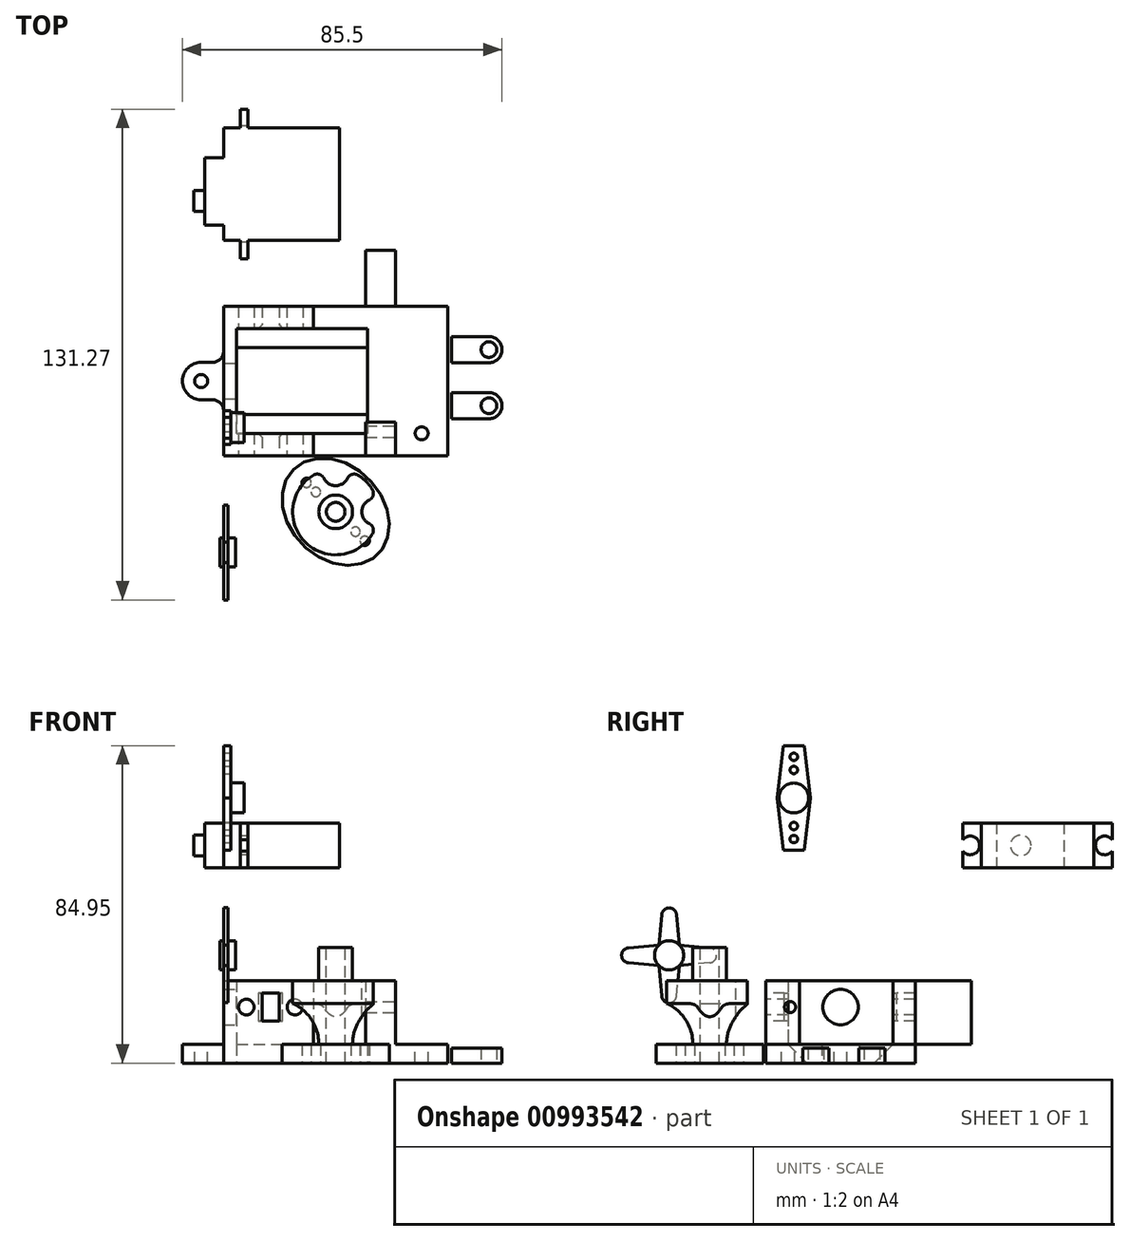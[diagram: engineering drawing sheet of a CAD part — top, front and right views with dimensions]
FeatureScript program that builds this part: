
annotation { "Feature Type Name" : "Feature", "Feature Type Description" : "" }
export const myFeature = defineFeature(function(context is Context, id is Id, definition is map)
    precondition{}
    {
        {
            assignVariable(context, id + "F0", {"variableType" : VariableType.LENGTH, "name" : "baseHgt", "lengthValue" : 17 * mm});
        }
        {
            assignVariable(context, id + "F1", {"variableType" : VariableType.LENGTH, "name" : "followerThk", "lengthValue" : 4 * mm});
        }
        {
            var Q0;
            Q0=qCreatedBy(makeId("Top.planeOp"),FACE);
            var sketch = newSketch(context, id + "F2", { "sketchPlane" : qUnion([Q0])});
            skLineSegment(sketch, "E0.bottom", {"start": v(0, 0) * mm, "end": v(60, 0) * mm});
            skLineSegment(sketch, "E0.top", {"start": v(0, 40) * mm, "end": v(60, 40) * mm});
            skLineSegment(sketch, "E0.left", {"start": v(0, 0) * mm, "end": v(0, 40) * mm});
            skLineSegment(sketch, "E0.right", {"start": v(60, 0) * mm, "end": v(60, 40) * mm});
            skLineSegment(sketch, "E1.bottom", {"start": v(30, 40) * mm, "end": v(60, 40) * mm});
            skLineSegment(sketch, "E1.top", {"start": v(30, 55) * mm, "end": v(60, 55) * mm});
            skLineSegment(sketch, "E1.left", {"start": v(30, 40) * mm, "end": v(30, 55) * mm});
            skLineSegment(sketch, "E1.right", {"start": v(60, 40) * mm, "end": v(60, 55) * mm});
            skLineSegment(sketch, "E2", {"start": v(0, 25) * mm, "end": v(-6, 25) * mm});
            skLineSegment(sketch, "E3", {"start": v(0, 15) * mm, "end": v(-6, 15) * mm});
            skArc(sketch, "E4", {"start": v(-6, 25) * mm, "mid": v(-11, 20) * mm, "end": v(-6, 15) * mm});
            skLineSegment(sketch, "E5", {"start": v(-6, 20) * mm, "end": v(0, 20) * mm, "construction": true});
            skSolve(sketch);
        }
        {
            var Q0;
            Q0=makeQuery(id+"F2.imprint","IMPRINT",FACE,{"disambiguationData":[TD([[makeQuery(id+"F2.imprint","IMPRINT",EDGE,{"derivedFrom":sQuery(id+"F2.wireOp",EDGE,"E0.bottom")}),1.0]])]});
            var Q1;
            Q1=makeQuery(id+"F2.imprint","IMPRINT",FACE,{"disambiguationData":[TD([[makeQuery(id+"F2.imprint","IMPRINT",EDGE,{"derivedFrom":sQuery(id+"F2.wireOp",EDGE,"E1.bottom")}),1.0]])]});
            var Q2;
            {var subQ0=sQuery(id+"F2.wireOp",EDGE,"E2");Q2=makeQuery(id+"F2.imprint","IMPRINT",FACE,{"disambiguationData":[TD([[makeQuery(id+"F2.imprint","IMPRINT",EDGE,{"derivedFrom":subQ0}),1.0]])]});}
            extrude(context, id + "F3", {"entities" : qUnion([Q0, Q1, Q2]), "depth" : 5 * mm, "offsetDistance" : 25 * mm});
        }
        {
            var Q0;
            Q0=makeQuery(id+"F3.opExtrude","CAP_FACE",FACE,{"disambiguationData":[OSD([sQuery(id+"F2.wireOp",EDGE,"E0.bottom"),sQuery(id+"F2.wireOp",EDGE,"E0.top"),sQuery(id+"F2.wireOp",EDGE,"E0.left"),sQuery(id+"F2.wireOp",EDGE,"E0.right")])],"isStart":false});
            var sketch = newSketch(context, id + "F4", { "sketchPlane" : qUnion([Q0])});
            skLineSegment(sketch, "E6", {"start": v(24, 0) * mm, "end": v(0, 0) * mm});
            skLineSegment(sketch, "E7", {"start": v(0, 0) * mm, "end": v(0, 40) * mm});
            skLineSegment(sketch, "E8", {"start": v(0, 40) * mm, "end": v(24, 40) * mm});
            skLineSegment(sketch, "E9", {"start": v(24, 40) * mm, "end": v(24, 34) * mm});
            skLineSegment(sketch, "E10", {"start": v(24, 34) * mm, "end": v(3.5, 34) * mm});
            skLineSegment(sketch, "E11", {"start": v(3.5, 34) * mm, "end": v(3.5, 6) * mm});
            skLineSegment(sketch, "E12", {"start": v(3.5, 6) * mm, "end": v(24, 6) * mm});
            skLineSegment(sketch, "E13", {"start": v(24, 6) * mm, "end": v(24, 0) * mm});
            skSolve(sketch);
        }
        {
            var Q0;
            Q0=makeQuery(id+"F4.imprint","IMPRINT",FACE,{"disambiguationData":[TD([[makeQuery(id+"F4.imprint","IMPRINT",EDGE,{"derivedFrom":sQuery(id+"F4.wireOp",EDGE,"E6")}),1.0]])]});
            extrude(context, id + "F5", {"entities" : qUnion([Q0]), "operationType" : NewBodyOperationType.ADD, "depth" : getVariable(context, 'baseHgt'), "offsetDistance" : 25 * mm});
        }
        {
            var Q0;
            Q0=makeQuery(id+"F5.opExtrude","SWEPT_FACE",FACE,{"disambiguationData":[OSD([sQuery(id+"F4.wireOp",EDGE,"E11")])]});
            var sketch = newSketch(context, id + "F6", { "sketchPlane" : qUnion([Q0])});
            skCircle(sketch, "E14", {"center": v(20, 15) * mm, "radius": 4.75 * mm});
            skLineSegment(sketch, "E15", {"start": v(20, 15) * mm, "end": v(20, 5) * mm, "construction": true});
            skSolve(sketch);
        }
        {
            var Q0;
            Q0 = qSketchRegion(id + "F6", true);
            extrude(context, id + "F7", {"entities" : qUnion([Q0]), "operationType" : NewBodyOperationType.REMOVE, "endBound" : BoundingType.THROUGH_ALL, "oppositeDirection" : true, "depth" : 25 * mm, "offsetDistance" : 25 * mm});
        }
        {
            var Q0;
            Q0=makeQuery(id+"F5.boolean.opBoolean","MERGE",FACE,{"derivedFrom":[makeQuery(id+"F3.opExtrude","SWEPT_FACE",FACE,{"disambiguationData":[OSD([sQuery(id+"F2.wireOp",EDGE,"E0.bottom")])]}),makeQuery(id+"F5.opExtrude","SWEPT_FACE",FACE,{"disambiguationData":[OSD([sQuery(id+"F4.wireOp",EDGE,"E6")])]})]});
            var sketch = newSketch(context, id + "F8", { "sketchPlane" : qUnion([Q0])});
            skLineSegment(sketch, "E16.bottom", {"start": v(10.35, 18.75) * mm, "end": v(14.85, 18.75) * mm});
            skLineSegment(sketch, "E16.top", {"start": v(10.35, 11.25) * mm, "end": v(14.85, 11.25) * mm});
            skLineSegment(sketch, "E16.left", {"start": v(10.35, 18.75) * mm, "end": v(10.35, 11.25) * mm});
            skLineSegment(sketch, "E16.right", {"start": v(14.85, 18.75) * mm, "end": v(14.85, 11.25) * mm});
            skLineSegment(sketch, "E17", {"start": v(10.35, 15) * mm, "end": v(6.1, 15) * mm, "construction": true});
            skLineSegment(sketch, "E18", {"start": v(14.85, 15) * mm, "end": v(19.1, 15) * mm, "construction": true});
            skCircle(sketch, "E19", {"center": v(6.1, 15) * mm, "radius": 2.1 * mm});
            skCircle(sketch, "E20", {"center": v(19.1, 15) * mm, "radius": 2.1 * mm});
            skLineSegment(sketch, "E21", {"start": v(4, 22) * mm, "end": v(4, 0) * mm, "construction": true});
            skLineSegment(sketch, "E22", {"start": v(3.5, 22) * mm, "end": v(3.5, 0) * mm, "construction": true});
            skSolve(sketch);
        }
        {
            var Q0;
            Q0 = qSketchRegion(id + "F8", true);
            extrude(context, id + "F9", {"entities" : qUnion([Q0]), "operationType" : NewBodyOperationType.REMOVE, "endBound" : BoundingType.THROUGH_ALL, "oppositeDirection" : true, "depth" : 25 * mm, "offsetDistance" : 25 * mm});
        }
        {
            var Q0;
            Q0=qCreatedBy(makeId("Right.planeOp"),FACE);
            var sketch = newSketch(context, id + "F10", { "sketchPlane" : qUnion([Q0])});
            skLineSegment(sketch, "E23.bottom", {"start": v(57.7, 52.25) * mm, "end": v(87.7, 52.25) * mm});
            skLineSegment(sketch, "E23.top", {"start": v(57.7, 64.25) * mm, "end": v(87.7, 64.25) * mm});
            skLineSegment(sketch, "E23.left", {"start": v(57.7, 52.25) * mm, "end": v(57.7, 64.25) * mm});
            skLineSegment(sketch, "E23.right", {"start": v(87.7, 52.25) * mm, "end": v(87.7, 64.25) * mm});
            skSolve(sketch);
        }
        {
            var Q0;
            Q0=makeQuery(id+"F10.imprint","IMPRINT",FACE,{"disambiguationData":[TD([[makeQuery(id+"F10.imprint","IMPRINT",EDGE,{"derivedFrom":sQuery(id+"F10.wireOp",EDGE,"E23.bottom")}),1.0]])]});
            extrude(context, id + "F11", {"entities" : qUnion([Q0]), "depth" : 31 * mm, "offsetDistance" : 25 * mm});
        }
        {
            var Q0;
            Q0=makeQuery(id+"F11.opExtrude","SWEPT_FACE",FACE,{"disambiguationData":[OSD([sQuery(id+"F10.wireOp",EDGE,"E23.left")])]});
            var sketch = newSketch(context, id + "F12", { "sketchPlane" : qUnion([Q0])});
            skLineSegment(sketch, "E24.bottom", {"start": v(4.5, 64.25) * mm, "end": v(6.5, 64.25) * mm});
            skLineSegment(sketch, "E24.top", {"start": v(4.5, 52.25) * mm, "end": v(6.5, 52.25) * mm});
            skLineSegment(sketch, "E24.left", {"start": v(4.5, 64.25) * mm, "end": v(4.5, 52.25) * mm});
            skLineSegment(sketch, "E24.right", {"start": v(6.5, 64.25) * mm, "end": v(6.5, 52.25) * mm});
            skSolve(sketch);
        }
        {
            var Q0;
            Q0 = qSketchRegion(id + "F12", true);
            extrude(context, id + "F13", {"entities" : qUnion([Q0]), "operationType" : NewBodyOperationType.ADD, "depth" : 5 * mm, "offsetDistance" : 25 * mm, "hasSecondDirection" : true, "secondDirectionOppositeDirection" : true, "secondDirectionDepth" : 35 * mm});
        }
        {
            var Q0;
            Q0=makeQuery(id+"F11.opExtrude","CAP_FACE",FACE,{"disambiguationData":[OSD([sQuery(id+"F10.wireOp",EDGE,"E23.bottom"),sQuery(id+"F10.wireOp",EDGE,"E23.top"),sQuery(id+"F10.wireOp",EDGE,"E23.left"),sQuery(id+"F10.wireOp",EDGE,"E23.right")])],"isStart":true});
            var sketch = newSketch(context, id + "F14", { "sketchPlane" : qUnion([Q0])});
            skLineSegment(sketch, "E25.bottom", {"start": v(-79.7, 64.25) * mm, "end": v(-61.7, 64.25) * mm});
            skLineSegment(sketch, "E25.top", {"start": v(-79.7, 52.25) * mm, "end": v(-61.7, 52.25) * mm});
            skLineSegment(sketch, "E25.left", {"start": v(-79.7, 64.25) * mm, "end": v(-79.7, 52.25) * mm});
            skLineSegment(sketch, "E25.right", {"start": v(-61.7, 64.25) * mm, "end": v(-61.7, 52.25) * mm});
            skSolve(sketch);
        }
        {
            var Q0;
            Q0=makeQuery(id+"F14.imprint","IMPRINT",FACE,{"disambiguationData":[TD([[makeQuery(id+"F14.imprint","IMPRINT",EDGE,{"derivedFrom":sQuery(id+"F14.wireOp",EDGE,"E25.bottom")}),1.0]])]});
            extrude(context, id + "F15", {"entities" : qUnion([Q0]), "operationType" : NewBodyOperationType.ADD, "depth" : 5 * mm, "offsetDistance" : 25 * mm});
        }
        {
            var Q0;
            Q0=makeQuery(id+"F15.opExtrude","CAP_FACE",FACE,{"disambiguationData":[OSD([sQuery(id+"F14.wireOp",EDGE,"E25.bottom"),sQuery(id+"F14.wireOp",EDGE,"E25.top"),sQuery(id+"F14.wireOp",EDGE,"E25.left"),sQuery(id+"F14.wireOp",EDGE,"E25.right")])],"isStart":false});
            var sketch = newSketch(context, id + "F16", { "sketchPlane" : qUnion([Q0])});
            skCircle(sketch, "E26", {"center": v(-68.2, 58.25) * mm, "radius": 2.75 * mm});
            skLineSegment(sketch, "E27", {"start": v(-79.7, 58.25) * mm, "end": v(-68.2, 58.25) * mm, "construction": true});
            skLineSegment(sketch, "E28.0", {"start": v(-57.7, 52.25) * mm, "end": v(-57.7, 64.25) * mm, "construction": true});
            skSolve(sketch);
        }
        {
            var Q0;
            Q0=makeQuery(id+"F16.imprint","IMPRINT",FACE,{"disambiguationData":[TD([[makeQuery(id+"F16.imprint","IMPRINT",EDGE,{"derivedFrom":sQuery(id+"F16.wireOp",EDGE,"E26")}),1.0]])]});
            extrude(context, id + "F17", {"entities" : qUnion([Q0]), "operationType" : NewBodyOperationType.ADD, "depth" : 3 * mm, "offsetDistance" : 25 * mm});
        }
        {
            var Q0;
            Q0=qCreatedBy(makeId("Right.planeOp"),FACE);
            var sketch = newSketch(context, id + "F18", { "sketchPlane" : qUnion([Q0])});
            skLineSegment(sketch, "E29", {"start": v(-27.87, 39.72) * mm, "end": v(-28.62, 31.6) * mm});
            skLineSegment(sketch, "E30", {"start": v(-25.87, 41.55) * mm, "end": v(-25.87, 28.85) * mm});
            skArc(sketch, "E31", {"start": v(-25.87, 41.55) * mm, "mid": v(-27.22, 41.02) * mm, "end": v(-27.87, 39.72) * mm});
            skLineSegment(sketch, "E32", {"start": v(-25.87, 28.85) * mm, "end": v(-38.57, 28.85) * mm});
            skArc(sketch, "E33", {"start": v(-36.74, 30.85) * mm, "mid": v(-38.04, 30.2) * mm, "end": v(-38.57, 28.85) * mm});
            skLineSegment(sketch, "E34", {"start": v(-25.87, 41.55) * mm, "end": v(-19.8, 41.55) * mm, "construction": true});
            skLineSegment(sketch, "E35", {"start": v(-38.57, 28.85) * mm, "end": v(-38.57, 21.53) * mm, "construction": true});
            skLineSegment(sketch, "E36", {"start": v(-36.74, 30.85) * mm, "end": v(-28.62, 31.6) * mm});
            skCircle(sketch, "E37", {"center": v(-25.87, 28.85) * mm, "radius": 12.7 * mm, "construction": true});
            skSolve(sketch);
        }
        {
            var Q0;
            Q0=makeQuery(id+"F18.imprint","IMPRINT",FACE,{"disambiguationData":[TD([[makeQuery(id+"F18.imprint","IMPRINT",EDGE,{"derivedFrom":sQuery(id+"F18.wireOp",EDGE,"E29")}),1.0]])]});
            extrude(context, id + "F19", {"entities" : qUnion([Q0]), "depth" : 1.2 * mm, "offsetDistance" : 25 * mm});
        }
        {
            var Q0;
            Q0=makeQuery(id+"F19.opExtrude","SWEPT_BODY",BODY,{"disambiguationData":[OSD([sQuery(id+"F18.wireOp",EDGE,"E29"),sQuery(id+"F18.wireOp",EDGE,"E30"),sQuery(id+"F18.wireOp",EDGE,"E31"),sQuery(id+"F18.wireOp",EDGE,"E32"),sQuery(id+"F18.wireOp",EDGE,"E33"),sQuery(id+"F18.wireOp",EDGE,"E36")])]});
            var Q1;
            Q1=makeQuery(id+"F19.opExtrude","SWEPT_EDGE",EDGE,{"disambiguationData":[OSD([sQuery(id+"F18.wireOp",EDGE,"E30"),sQuery(id+"F18.wireOp",EDGE,"E32")])]});
            circularPattern(context, id + "F20", {"operationType" : NewBodyOperationType.ADD, "entities" : qUnion([Q0]), "axis" : qUnion([Q1]), "angle" : 360 * degree, "instanceCount" : 4, "equalSpace" : true});
        }
        {
            var Q0;
            {var subQ0=makeQuery(id+"F19.opExtrude","CAP_FACE",FACE,{"disambiguationData":[OSD([sQuery(id+"F18.wireOp",EDGE,"E29"),sQuery(id+"F18.wireOp",EDGE,"E30"),sQuery(id+"F18.wireOp",EDGE,"E31"),sQuery(id+"F18.wireOp",EDGE,"E32"),sQuery(id+"F18.wireOp",EDGE,"E33"),sQuery(id+"F18.wireOp",EDGE,"E36")])],"isStart":false});Q0=makeQuery(id+"F20.boolean.opBoolean","MERGE",FACE,{"derivedFrom":[subQ0,makeQuery(id+"F20.opPattern","COPY",FACE,{"derivedFrom":subQ0,"instanceName":"1"}),makeQuery(id+"F20.opPattern","COPY",FACE,{"derivedFrom":subQ0,"instanceName":"2"}),makeQuery(id+"F20.opPattern","COPY",FACE,{"derivedFrom":subQ0,"instanceName":"3"})]});}
            var sketch = newSketch(context, id + "F21", { "sketchPlane" : qUnion([Q0])});
            skLineSegment(sketch, "E38", {"start": v(-23.12, 31.6) * mm, "end": v(-28.62, 26.1) * mm, "construction": true});
            skCircle(sketch, "E39", {"center": v(-25.87, 28.85) * mm, "radius": 3.9 * mm});
            skSolve(sketch);
        }
        {
            var Q0;
            Q0 = qSketchRegion(id + "F21", true);
            extrude(context, id + "F22", {"entities" : qUnion([Q0]), "operationType" : NewBodyOperationType.ADD, "depth" : 2 * mm, "offsetDistance" : 25 * mm, "hasSecondDirection" : true, "secondDirectionOppositeDirection" : true, "secondDirectionDepth" : 2.2 * mm});
        }
        {
            var Q0;
            {var subQ1=sQuery(id+"F12.wireOp",EDGE,"E24.left");Q0=makeQuery(id+"F13.boolean.opBoolean","SPLIT",FACE,{"disambiguationData":[TD([makeQuery(id+"F11.opExtrude","SWEPT_FACE",FACE,{"disambiguationData":[OSD([sQuery(id+"F10.wireOp",EDGE,"E23.right")])]})])],"derivedFrom":makeQuery(id+"F13.opExtrude","SWEPT_FACE",FACE,{"disambiguationData":[OSD([subQ1])]})});}
            var sketch = newSketch(context, id + "F23", { "sketchPlane" : qUnion([Q0])});
            skPoint(sketch, "E40", {"position": v(-90.7, 58.25) * mm});
            skPoint(sketch, "E41", {"position": v(-54.7, 58.25) * mm});
            skLineSegment(sketch, "E42", {"start": v(-92.7, 58.25) * mm, "end": v(-90.7, 58.25) * mm, "construction": true});
            skLineSegment(sketch, "E43.0", {"start": v(-52.7, 64.25) * mm, "end": v(-52.7, 52.25) * mm, "construction": true});
            skLineSegment(sketch, "E44", {"start": v(-54.7, 58.25) * mm, "end": v(-52.7, 58.25) * mm, "construction": true});
            skCircle(sketch, "E45", {"center": v(-90.7, 58.25) * mm, "radius": 2.5 * mm});
            skCircle(sketch, "E46", {"center": v(-54.7, 58.25) * mm, "radius": 2.5 * mm});
            skSolve(sketch);
        }
        {
            var Q0;
            {var subQ0=sQuery(id+"F23.wireOp",EDGE,"E45");var subQ1=makeQuery(id+"F13.opExtrude","CAP_EDGE",EDGE,{"disambiguationData":[OSD([sQuery(id+"F12.wireOp",EDGE,"E24.left")])],"isStart":true});var subQ2=makeQuery(id+"F23.imprint","INTERSECT",VERTEX,{"disambiguationData":[OD(0.0)],"derivedFrom":[subQ1,subQ0]});Q0=makeQuery(id+"F23.imprint","IMPRINT",FACE,{"disambiguationData":[TD([[makeQuery(id+"F23.imprint","IMPRINT",EDGE,{"disambiguationData":[TD([[subQ2,1.0]])],"derivedFrom":subQ0}),1.0]])]});}
            var Q1;
            Q1=makeQuery(id+"F23.imprint","IMPRINT",FACE,{"disambiguationData":[TD([[makeQuery(id+"F23.imprint","IMPRINT",EDGE,{"derivedFrom":sQuery(id+"F23.wireOp",EDGE,"E46")}),1.0]])]});
            extrude(context, id + "F24", {"entities" : qUnion([Q0, Q1]), "operationType" : NewBodyOperationType.REMOVE, "endBound" : BoundingType.THROUGH_ALL, "oppositeDirection" : true, "depth" : 25 * mm, "offsetDistance" : 25 * mm});
        }
        {
            var Q0;
            Q0=makeQuery(id+"F3.opExtrude","CAP_FACE",FACE,{"disambiguationData":[OSD([sQuery(id+"F2.wireOp",EDGE,"E0.bottom"),sQuery(id+"F2.wireOp",EDGE,"E0.top"),sQuery(id+"F2.wireOp",EDGE,"E0.left"),sQuery(id+"F2.wireOp",EDGE,"E0.right"),sQuery(id+"F2.wireOp",EDGE,"E1.top"),sQuery(id+"F2.wireOp",EDGE,"E1.left"),sQuery(id+"F2.wireOp",EDGE,"E1.right")])],"isStart":false});
            var sketch = newSketch(context, id + "F25", { "sketchPlane" : qUnion([Q0])});
            skLineSegment(sketch, "E47.bottom", {"start": v(38, 0) * mm, "end": v(46, 0) * mm});
            skLineSegment(sketch, "E47.top", {"start": v(38, 9) * mm, "end": v(46, 9) * mm});
            skLineSegment(sketch, "E47.left", {"start": v(38, 0) * mm, "end": v(38, 9) * mm});
            skLineSegment(sketch, "E47.right", {"start": v(46, 0) * mm, "end": v(46, 9) * mm});
            skLineSegment(sketch, "E48.bottom", {"start": v(38, 55) * mm, "end": v(46, 55) * mm});
            skLineSegment(sketch, "E48.top", {"start": v(38, 40) * mm, "end": v(46, 40) * mm});
            skLineSegment(sketch, "E48.left", {"start": v(38, 55) * mm, "end": v(38, 40) * mm});
            skLineSegment(sketch, "E48.right", {"start": v(46, 55) * mm, "end": v(46, 40) * mm});
            skSolve(sketch);
        }
        {
            var Q0;
            Q0=makeQuery(id+"F25.imprint","IMPRINT",FACE,{"disambiguationData":[TD([[makeQuery(id+"F25.imprint","IMPRINT",EDGE,{"derivedFrom":sQuery(id+"F25.wireOp",EDGE,"E47.bottom")}),1.0]])]});
            var Q1;
            Q1=makeQuery(id+"F25.imprint","IMPRINT",FACE,{"disambiguationData":[TD([[makeQuery(id+"F25.imprint","IMPRINT",EDGE,{"derivedFrom":sQuery(id+"F25.wireOp",EDGE,"E48.bottom")}),-1.0]])]});
            extrude(context, id + "F26", {"entities" : qUnion([Q0, Q1]), "operationType" : NewBodyOperationType.ADD, "depth" : getVariable(context, 'baseHgt'), "offsetDistance" : 25 * mm});
        }
        {
            var Q0;
            Q0=qCreatedBy(makeId("Right.planeOp"),FACE);
            var sketch = newSketch(context, id + "F27", { "sketchPlane" : qUnion([Q0])});
            skLineSegment(sketch, "E49", {"start": v(5.72, 92.95) * mm, "end": v(9.28, 92.95) * mm, "construction": true});
            skLineSegment(sketch, "E50", {"start": v(3, 70.95) * mm, "end": v(12, 70.95) * mm, "construction": true});
            skLineSegment(sketch, "E51", {"start": v(7.5, 92.95) * mm, "end": v(7.5, 70.95) * mm, "construction": true});
            skLineSegment(sketch, "E52", {"start": v(3, 70.95) * mm, "end": v(4.73, 84.95) * mm});
            skLineSegment(sketch, "E53", {"start": v(4.73, 84.95) * mm, "end": v(5.72, 92.95) * mm, "construction": true});
            skLineSegment(sketch, "E54", {"start": v(12, 70.95) * mm, "end": v(10.27, 84.95) * mm});
            skLineSegment(sketch, "E55", {"start": v(10.27, 84.95) * mm, "end": v(9.28, 92.95) * mm, "construction": true});
            skArc(sketch, "E56", {"start": v(9.5, 91.18) * mm, "mid": v(7.5, 92.95) * mm, "end": v(5.5, 91.18) * mm, "construction": true});
            skLineSegment(sketch, "E57.MirrorCS", {"start": v(3, 70.95) * mm, "end": v(4.73, 56.95) * mm});
            skLineSegment(sketch, "E58.MirrorCS", {"start": v(12, 70.95) * mm, "end": v(10.27, 56.95) * mm});
            skLineSegment(sketch, "E59", {"start": v(4.73, 56.95) * mm, "end": v(10.27, 56.95) * mm});
            skLineSegment(sketch, "E60", {"start": v(4.73, 84.95) * mm, "end": v(10.27, 84.95) * mm});
            skSolve(sketch);
        }
        {
            var Q0;
            Q0 = qSketchRegion(id + "F27", true);
            extrude(context, id + "F28", {"entities" : qUnion([Q0]), "depth" : 2 * mm, "offsetDistance" : 25 * mm});
        }
        {
            var Q0;
            Q0=makeQuery(id+"F28.opExtrude","CAP_FACE",FACE,{"disambiguationData":[OSD([sQuery(id+"F27.wireOp",EDGE,"E52"),sQuery(id+"F27.wireOp",EDGE,"E54"),sQuery(id+"F27.wireOp",EDGE,"E57.MirrorCS"),sQuery(id+"F27.wireOp",EDGE,"E58.MirrorCS"),sQuery(id+"F27.wireOp",EDGE,"E59"),sQuery(id+"F27.wireOp",EDGE,"E60")])],"isStart":false});
            var sketch = newSketch(context, id + "F29", { "sketchPlane" : qUnion([Q0])});
            skLineSegment(sketch, "E61", {"start": v(7.5, 84.95) * mm, "end": v(7.5, 56.95) * mm, "construction": true});
            skPoint(sketch, "E62", {"position": v(7.5, 78.45) * mm});
            skPoint(sketch, "E63", {"position": v(7.5, 63.45) * mm});
            skLineSegment(sketch, "E64", {"start": v(3, 70.95) * mm, "end": v(12, 70.95) * mm, "construction": true});
            skCircle(sketch, "E65", {"center": v(7.5, 78.45) * mm, "radius": 1 * mm});
            skCircle(sketch, "E66", {"center": v(7.5, 63.45) * mm, "radius": 1 * mm});
            skCircle(sketch, "E67", {"center": v(7.5, 81.95) * mm, "radius": 1 * mm});
            skCircle(sketch, "E68", {"center": v(7.5, 59.95) * mm, "radius": 1 * mm});
            skSolve(sketch);
        }
        {
            var Q0;
            Q0 = qSketchRegion(id + "F29", true);
            extrude(context, id + "F30", {"entities" : qUnion([Q0]), "operationType" : NewBodyOperationType.REMOVE, "endBound" : BoundingType.THROUGH_ALL, "oppositeDirection" : true, "depth" : 25 * mm, "offsetDistance" : 25 * mm});
        }
        {
            var Q0;
            Q0=makeQuery(id+"F28.opExtrude","CAP_FACE",FACE,{"disambiguationData":[OSD([sQuery(id+"F27.wireOp",EDGE,"E52"),sQuery(id+"F27.wireOp",EDGE,"E54"),sQuery(id+"F27.wireOp",EDGE,"E57.MirrorCS"),sQuery(id+"F27.wireOp",EDGE,"E58.MirrorCS"),sQuery(id+"F27.wireOp",EDGE,"E59"),sQuery(id+"F27.wireOp",EDGE,"E60")])],"isStart":false});
            var sketch = newSketch(context, id + "F31", { "sketchPlane" : qUnion([Q0])});
            skCircle(sketch, "E69", {"center": v(7.5, 70.95) * mm, "radius": 4 * mm});
            skPoint(sketch, "E69.centerSnap0", {"position": v(7.5, 84.95) * mm});
            skSolve(sketch);
        }
        {
            var Q0;
            Q0 = qSketchRegion(id + "F31", true);
            extrude(context, id + "F32", {"entities" : qUnion([Q0]), "operationType" : NewBodyOperationType.ADD, "depth" : 3.5 * mm, "offsetDistance" : 25 * mm});
        }
        {
            assignVariable(context, id + "F33", {"variableType" : VariableType.LENGTH, "name" : "camIndentFillet", "lengthValue" : 2 * mm});
        }
        {
            var Q0;
            Q0=qCreatedBy(makeId("Front.planeOp"),FACE);
            cPlane(context, id + "F34", {"entities" : qUnion([Q0]), "cplaneType" : CPlaneType.OFFSET, "offset" : 15 * mm, "width" : 150 * mm, "height" : 150 * mm});
        }
        {
            var Q0;
            Q0=qCreatedBy(id+"F34.planeOp",FACE);
            var sketch = newSketch(context, id + "F35", { "sketchPlane" : qUnion([Q0])});
            skLineSegment(sketch, "E70", {"start": v(30, 0) * mm, "end": v(42.5, 0) * mm});
            skLineSegment(sketch, "E71", {"start": v(42.5, 0) * mm, "end": v(42.5, 5) * mm});
            skLineSegment(sketch, "E72", {"start": v(42.5, 5) * mm, "end": v(34.5, 5) * mm});
            skArc(sketch, "E73", {"start": v(41.5, 16) * mm, "mid": v(36.4, 11.52) * mm, "end": v(34.5, 5) * mm});
            skLineSegment(sketch, "E74", {"start": v(34.5, 5) * mm, "end": v(34.5, 13) * mm, "construction": true});
            skLineSegment(sketch, "E75", {"start": v(41.5, 16) * mm, "end": v(41.5, 22) * mm});
            skLineSegment(sketch, "E76", {"start": v(41.5, 22) * mm, "end": v(34.5, 22) * mm});
            skLineSegment(sketch, "E77", {"start": v(34.5, 22) * mm, "end": v(34.5, 31) * mm});
            skLineSegment(sketch, "E78", {"start": v(30, 0) * mm, "end": v(30, 31) * mm});
            skLineSegment(sketch, "E79", {"start": v(30, 31) * mm, "end": v(34.5, 31) * mm});
            skSolve(sketch);
        }
        {
            var Q0;
            Q0 = qSketchRegion(id + "F35", true);
            var Q1;
            Q1=sQuery(id+"F35.wireOp",EDGE,"E78");
            revolve(context, id + "F36", {"surfaceOperationType" : NewSurfaceOperationType.NEW, "entities" : qUnion([Q0]), "axis" : qUnion([Q1]), "revolveType" : RevolveType.FULL});
        }
        {
            var Q0;
            Q0=makeQuery(id+"F36.opRevolve","SWEPT_FACE",FACE,{"disambiguationData":[OSD([sQuery(id+"F35.wireOp",EDGE,"E76")])]});
            var sketch = newSketch(context, id + "F37", { "sketchPlane" : qUnion([Q0])});
            skCircle(sketch, "E80", {"center": v(30, -4.5) * mm, "radius": 3.5 * mm});
            skCircle(sketch, "E81", {"center": v(40.5, -15) * mm, "radius": 3.5 * mm});
            skLineSegment(sketch, "E82", {"start": v(30, -4.5) * mm, "end": v(30, -15) * mm, "construction": true});
            skLineSegment(sketch, "E83", {"start": v(30, -15) * mm, "end": v(40.5, -15) * mm, "construction": true});
            skSolve(sketch);
        }
        {
            var Q0;
            Q0 = qSketchRegion(id + "F37", true);
            var Q1;
            Q1=makeQuery(id+"F36.opRevolve","SWEPT_FACE",FACE,{"disambiguationData":[OSD([sQuery(id+"F35.wireOp",EDGE,"E73")])]});
            extrude(context, id + "F38", {"entities" : qUnion([Q0]), "operationType" : NewBodyOperationType.REMOVE, "endBound" : BoundingType.UP_TO_SURFACE, "oppositeDirection" : true, "depth" : 25 * mm, "endBoundEntityFace" : qUnion([Q1]), "offsetDistance" : 25 * mm});
        }
        {
            var Q0;
            Q0=makeQuery(id+"F38.boolean.opBoolean","INTERSECT",EDGE,{"disambiguationData":[OD(0.0)],"derivedFrom":[makeQuery(id+"F36.opRevolve","SWEPT_FACE",FACE,{"disambiguationData":[OSD([sQuery(id+"F35.wireOp",EDGE,"E75")])]}),makeQuery(id+"F38.opExtrude","SWEPT_FACE",FACE,{"disambiguationData":[OSD([sQuery(id+"F37.wireOp",EDGE,"E80")])]})]});
            var Q1;
            Q1=makeQuery(id+"F38.boolean.opBoolean","INTERSECT",EDGE,{"disambiguationData":[OD(1.0)],"derivedFrom":[makeQuery(id+"F36.opRevolve","SWEPT_FACE",FACE,{"disambiguationData":[OSD([sQuery(id+"F35.wireOp",EDGE,"E75")])]}),makeQuery(id+"F38.opExtrude","SWEPT_FACE",FACE,{"disambiguationData":[OSD([sQuery(id+"F37.wireOp",EDGE,"E80")])]})]});
            var Q2;
            Q2=makeQuery(id+"F38.boolean.opBoolean","INTERSECT",EDGE,{"disambiguationData":[OD(0.0)],"derivedFrom":[makeQuery(id+"F36.opRevolve","SWEPT_FACE",FACE,{"disambiguationData":[OSD([sQuery(id+"F35.wireOp",EDGE,"E75")])]}),makeQuery(id+"F38.opExtrude","SWEPT_FACE",FACE,{"disambiguationData":[OSD([sQuery(id+"F37.wireOp",EDGE,"E81")])]})]});
            var Q3;
            Q3=makeQuery(id+"F38.boolean.opBoolean","INTERSECT",EDGE,{"disambiguationData":[OD(1.0)],"derivedFrom":[makeQuery(id+"F36.opRevolve","SWEPT_FACE",FACE,{"disambiguationData":[OSD([sQuery(id+"F35.wireOp",EDGE,"E75")])]}),makeQuery(id+"F38.opExtrude","SWEPT_FACE",FACE,{"disambiguationData":[OSD([sQuery(id+"F37.wireOp",EDGE,"E81")])]})]});
            fillet(context, id + "F39", {"entities" : qUnion([Q0, Q1, Q2, Q3]), "radius" : getVariable(context, 'camIndentFillet'), "tangentPropagation" : true, "allowEdgeOverflow" : false});
        }
        {
            var Q0;
            Q0=makeQuery(id+"F36.opRevolve","SWEPT_FACE",FACE,{"disambiguationData":[OSD([sQuery(id+"F35.wireOp",EDGE,"E70")])]});
            var sketch = newSketch(context, id + "F40", { "sketchPlane" : qUnion([Q0])});
            skEllipse(sketch, "E84", {"center": v(30, 15) * mm, "majorRadius": 12.5 * mm, "minorRadius": 16 * mm, "majorAxis": v(-0.7, 0.7)});
            skLineSegment(sketch, "E85", {"start": v(30, 15) * mm, "end": v(38.84, 6.16) * mm, "construction": true});
            skLineSegment(sketch, "E86", {"start": v(30, 15) * mm, "end": v(18.69, 3.69) * mm, "construction": true});
            skLineSegment(sketch, "E87", {"start": v(30, 15) * mm, "end": v(-10, 15) * mm, "construction": true});
            skSolve(sketch);
        }
        {
            var Q0;
            Q0 = qSketchRegion(id + "F40", true);
            var Q1;
            Q1=makeQuery(id+"F36.opRevolve","SWEPT_FACE",FACE,{"disambiguationData":[OSD([sQuery(id+"F35.wireOp",EDGE,"E72")])]});
            extrude(context, id + "F41", {"entities" : qUnion([Q0]), "operationType" : NewBodyOperationType.ADD, "endBound" : BoundingType.UP_TO_SURFACE, "oppositeDirection" : true, "depth" : 25 * mm, "endBoundEntityFace" : qUnion([Q1]), "offsetDistance" : 25 * mm});
        }
        {
            var Q0;
            Q0=makeQuery(id+"F36.opRevolve","SWEPT_FACE",FACE,{"disambiguationData":[OSD([sQuery(id+"F35.wireOp",EDGE,"E79")])]});
            var sketch = newSketch(context, id + "F42", { "sketchPlane" : qUnion([Q0])});
            skCircle(sketch, "E88", {"center": v(30, -15) * mm, "radius": 2.5 * mm});
            skSolve(sketch);
        }
        {
            var Q0;
            Q0 = qSketchRegion(id + "F42", true);
            extrude(context, id + "F43", {"entities" : qUnion([Q0]), "operationType" : NewBodyOperationType.REMOVE, "endBound" : BoundingType.THROUGH_ALL, "oppositeDirection" : true, "depth" : 25 * mm, "offsetDistance" : 25 * mm});
        }
        {
            var Q0;
            Q0=makeQuery(id+"F41.boolean.opBoolean","MERGE",FACE,{"derivedFrom":[makeQuery(id+"F36.opRevolve","SWEPT_FACE",FACE,{"disambiguationData":[OSD([sQuery(id+"F35.wireOp",EDGE,"E70")])]}),makeQuery(id+"F41.opExtrude","CAP_FACE",FACE,{"disambiguationData":[OSD([sQuery(id+"F40.wireOp",EDGE,"E84")])],"isStart":true})]});
            var sketch = newSketch(context, id + "F44", { "sketchPlane" : qUnion([Q0])});
            skLineSegment(sketch, "E89", {"start": v(41.31, 26.31) * mm, "end": v(18.69, 3.69) * mm, "construction": true});
            skLineSegment(sketch, "E90", {"start": v(21.16, 23.84) * mm, "end": v(38.84, 6.16) * mm, "construction": true});
            skPoint(sketch, "E91", {"position": v(22.22, 7.22) * mm});
            skPoint(sketch, "E92", {"position": v(37.78, 22.78) * mm});
            skPoint(sketch, "E93", {"position": v(35.3, 20.3) * mm});
            skPoint(sketch, "E94", {"position": v(24.7, 9.7) * mm});
            skSolve(sketch);
        }
        {
            var Q0;
            Q0=sQuery(id+"F44.wireOp",VERTEX,"E91");
            var Q1;
            Q1=sQuery(id+"F44.wireOp",VERTEX,"E92");
            var Q2;
            Q2=sQuery(id+"F44.wireOp",VERTEX,"E93");
            var Q3;
            Q3=sQuery(id+"F44.wireOp",VERTEX,"E94");
            var Q4;
            Q4=makeQuery(id+"F36.opRevolve","SWEPT_BODY",BODY,{"disambiguationData":[OSD([sQuery(id+"F35.wireOp",EDGE,"E70"),sQuery(id+"F35.wireOp",EDGE,"E71"),sQuery(id+"F35.wireOp",EDGE,"E72"),sQuery(id+"F35.wireOp",EDGE,"E73"),sQuery(id+"F35.wireOp",EDGE,"E75"),sQuery(id+"F35.wireOp",EDGE,"E76"),sQuery(id+"F35.wireOp",EDGE,"E77"),sQuery(id+"F35.wireOp",EDGE,"E78"),sQuery(id+"F35.wireOp",EDGE,"E79")])]});
            hole(context, id + "F45", {"style" : HoleStyle.SIMPLE, "endStyle" : HoleEndStyle.BLIND, "holeDiameter" : 2.5 * mm, "majorDiameter" : 5 * mm, "holeDepth" : 6 * mm, "isTappedThrough" : true, "tappedDepth" : 12 * mm, "tapClearance" : 3, "locations" : qUnion([Q0, Q1, Q2, Q3]), "scope" : qUnion([Q4])});
        }
        {
            var Q0;
            Q0=qCreatedBy(makeId("Top.planeOp"),FACE);
            var sketch = newSketch(context, id + "F46", { "sketchPlane" : qUnion([Q0])});
            skLineSegment(sketch, "E95", {"start": v(61, 9.9) * mm, "end": v(71, 9.9) * mm});
            skArc(sketch, "E96", {"start": v(71, 9.9) * mm, "mid": v(74.5, 13.4) * mm, "end": v(71, 16.9) * mm});
            skLineSegment(sketch, "E97", {"start": v(71, 16.9) * mm, "end": v(61, 16.9) * mm});
            skLineSegment(sketch, "E98", {"start": v(61, 16.9) * mm, "end": v(61, 9.9) * mm});
            skCircle(sketch, "E99", {"center": v(71, 13.4) * mm, "radius": 2.1 * mm});
            skLineSegment(sketch, "E100.0.1.0", {"start": v(61, 24.9) * mm, "end": v(71, 24.9) * mm});
            skLineSegment(sketch, "E100.0.1.1", {"start": v(61, 31.9) * mm, "end": v(61, 24.9) * mm});
            skLineSegment(sketch, "E100.0.1.2", {"start": v(71, 31.9) * mm, "end": v(61, 31.9) * mm});
            skCircle(sketch, "E100.0.1.3", {"center": v(71, 28.4) * mm, "radius": 2.1 * mm});
            skArc(sketch, "E100.0.1.4", {"start": v(71, 24.9) * mm, "mid": v(74.5, 28.4) * mm, "end": v(71, 31.9) * mm});
            skLineSegment(sketch, "E100.direction1", {"start": v(61, 9.9) * mm, "end": v(87.27, 9.9) * mm, "construction": true});
            skLineSegment(sketch, "E100.direction2", {"start": v(61, 9.9) * mm, "end": v(61, 24.9) * mm, "construction": true});
            skSolve(sketch);
        }
        {
            var Q0;
            Q0 = qSketchRegion(id + "F46", true);
            extrude(context, id + "F47", {"entities" : qUnion([Q0]), "depth" : getVariable(context, 'followerThk'), "offsetDistance" : 25 * mm});
        }
        {
            var Q0;
            Q0=makeQuery(id+"F26.opExtrude","SWEPT_FACE",FACE,{"disambiguationData":[OSD([sQuery(id+"F25.wireOp",EDGE,"E48.right")])]});
            var sketch = newSketch(context, id + "F48", { "sketchPlane" : qUnion([Q0])});
            skPoint(sketch, "E101", {"position": v(6.5, 15) * mm});
            skPoint(sketch, "E102", {"position": v(42.5, 15) * mm});
            skCircle(sketch, "E103.0", {"center": v(20, 15) * mm, "radius": 4.75 * mm, "construction": true});
            skLineSegment(sketch, "E104", {"start": v(6.5, 15) * mm, "end": v(42.5, 15) * mm, "construction": true});
            skLineSegment(sketch, "E105.0", {"start": v(9, 22) * mm, "end": v(9, 5) * mm, "construction": true});
            skLineSegment(sketch, "E106.0", {"start": v(40, 22) * mm, "end": v(40, 5) * mm, "construction": true});
            skLineSegment(sketch, "E107", {"start": v(6.5, 15) * mm, "end": v(9, 22) * mm, "construction": true});
            skLineSegment(sketch, "E108", {"start": v(40, 22) * mm, "end": v(42.5, 15) * mm, "construction": true});
            skSolve(sketch);
        }
        {
            var Q0;
            Q0=sQuery(id+"F48.wireOp",VERTEX,"E101");
            var Q1;
            Q1=sQuery(id+"F48.wireOp",VERTEX,"E102");
            var Q2;
            Q2=makeQuery(id+"F3.opExtrude","SWEPT_BODY",BODY,{"disambiguationData":[OSD([sQuery(id+"F2.wireOp",EDGE,"E0.bottom"),sQuery(id+"F2.wireOp",EDGE,"E0.top"),sQuery(id+"F2.wireOp",EDGE,"E0.left"),sQuery(id+"F2.wireOp",EDGE,"E0.right"),sQuery(id+"F2.wireOp",EDGE,"E1.top"),sQuery(id+"F2.wireOp",EDGE,"E1.left"),sQuery(id+"F2.wireOp",EDGE,"E1.right")])]});
            hole(context, id + "F49", {"style" : HoleStyle.SIMPLE, "endStyle" : HoleEndStyle.BLIND, "holeDiameter" : 3 * mm, "majorDiameter" : 5 * mm, "holeDepth" : 8 * mm, "isTappedThrough" : true, "tappedDepth" : 12 * mm, "tapClearance" : 3, "locations" : qUnion([Q0, Q1]), "scope" : qUnion([Q2])});
        }
        {
            var Q0;
            Q0=makeQuery(id+"F9.boolean.opBoolean","INTERSECT",EDGE,{"derivedFrom":[makeQuery(id+"F5.opExtrude","SWEPT_FACE",FACE,{"disambiguationData":[OSD([sQuery(id+"F4.wireOp",EDGE,"E10")])]}),makeQuery(id+"F9.opExtrude","SWEPT_FACE",FACE,{"disambiguationData":[OSD([sQuery(id+"F8.wireOp",EDGE,"E16.left")])]})]});
            var Q1;
            Q1=makeQuery(id+"F9.boolean.opBoolean","INTERSECT",EDGE,{"derivedFrom":[makeQuery(id+"F5.opExtrude","SWEPT_FACE",FACE,{"disambiguationData":[OSD([sQuery(id+"F4.wireOp",EDGE,"E10")])]}),makeQuery(id+"F9.opExtrude","SWEPT_FACE",FACE,{"disambiguationData":[OSD([sQuery(id+"F8.wireOp",EDGE,"E16.right")])]})]});
            var Q2;
            Q2=makeQuery(id+"F9.boolean.opBoolean","INTERSECT",EDGE,{"derivedFrom":[makeQuery(id+"F5.opExtrude","SWEPT_FACE",FACE,{"disambiguationData":[OSD([sQuery(id+"F4.wireOp",EDGE,"E12")])]}),makeQuery(id+"F9.opExtrude","SWEPT_FACE",FACE,{"disambiguationData":[OSD([sQuery(id+"F8.wireOp",EDGE,"E16.left")])]})]});
            var Q3;
            Q3=makeQuery(id+"F9.boolean.opBoolean","INTERSECT",EDGE,{"derivedFrom":[makeQuery(id+"F5.opExtrude","SWEPT_FACE",FACE,{"disambiguationData":[OSD([sQuery(id+"F4.wireOp",EDGE,"E12")])]}),makeQuery(id+"F9.opExtrude","SWEPT_FACE",FACE,{"disambiguationData":[OSD([sQuery(id+"F8.wireOp",EDGE,"E16.right")])]})]});
            chamfer(context, id + "F50", {"entities" : qUnion([Q0, Q1, Q2, Q3]), "width" : 1 * mm, "tangentPropagation" : true});
        }
        {
            var Q0;
            Q0=makeQuery(id+"F3.opExtrude","CAP_FACE",FACE,{"disambiguationData":[OSD([sQuery(id+"F2.wireOp",EDGE,"E0.bottom"),sQuery(id+"F2.wireOp",EDGE,"E0.top"),sQuery(id+"F2.wireOp",EDGE,"E0.left"),sQuery(id+"F2.wireOp",EDGE,"E0.right"),sQuery(id+"F2.wireOp",EDGE,"E1.top"),sQuery(id+"F2.wireOp",EDGE,"E1.left"),sQuery(id+"F2.wireOp",EDGE,"E1.right")])],"isStart":false});
            var sketch = newSketch(context, id + "F51", { "sketchPlane" : qUnion([Q0])});
            skPoint(sketch, "E109", {"position": v(53, 49) * mm});
            skPoint(sketch, "E109.positionSnap0", {"position": v(53, 55) * mm});
            skPoint(sketch, "E110", {"position": v(53, 6) * mm});
            skPoint(sketch, "E110.positionSnap0", {"position": v(53, 0) * mm});
            skLineSegment(sketch, "E111", {"start": v(53, 55) * mm, "end": v(53, 49) * mm, "construction": true});
            skLineSegment(sketch, "E112", {"start": v(53, 6) * mm, "end": v(53, 0) * mm, "construction": true});
            skPoint(sketch, "E113", {"position": v(-6, 20) * mm});
            skArc(sketch, "E114.0", {"start": v(-6, 25) * mm, "mid": v(-11, 20) * mm, "end": v(-6, 15) * mm, "construction": true});
            skSolve(sketch);
        }
        {
            var Q0;
            Q0=sQuery(id+"F51.wireOp",VERTEX,"E109");
            var Q1;
            Q1=sQuery(id+"F51.wireOp",VERTEX,"E110");
            var Q2;
            Q2=sQuery(id+"F51.wireOp",VERTEX,"E113");
            var Q3;
            Q3=makeQuery(id+"F3.opExtrude","SWEPT_BODY",BODY,{"disambiguationData":[OSD([sQuery(id+"F2.wireOp",EDGE,"E0.bottom"),sQuery(id+"F2.wireOp",EDGE,"E0.top"),sQuery(id+"F2.wireOp",EDGE,"E0.left"),sQuery(id+"F2.wireOp",EDGE,"E0.right"),sQuery(id+"F2.wireOp",EDGE,"E1.top"),sQuery(id+"F2.wireOp",EDGE,"E1.left"),sQuery(id+"F2.wireOp",EDGE,"E1.right")])]});
            hole(context, id + "F52", {"style" : HoleStyle.SIMPLE, "endStyle" : HoleEndStyle.THROUGH, "holeDiameter" : 3.5 * mm, "majorDiameter" : 5 * mm, "isTappedThrough" : true, "tappedDepth" : 12 * mm, "tapClearance" : 3, "locations" : qUnion([Q0, Q1, Q2]), "scope" : qUnion([Q3])});
        }
        {
            var Q0;
            Q0=makeQuery(id+"F3.opExtrude","SWEPT_EDGE",EDGE,{"disambiguationData":[OSD([sQuery(id+"F2.wireOp",EDGE,"E0.left"),sQuery(id+"F2.wireOp",EDGE,"E3")])]});
            var Q1;
            Q1=makeQuery(id+"F3.opExtrude","SWEPT_EDGE",EDGE,{"disambiguationData":[OSD([sQuery(id+"F2.wireOp",EDGE,"E0.left"),sQuery(id+"F2.wireOp",EDGE,"E2")])]});
            fillet(context, id + "F53", {"entities" : qUnion([Q0, Q1]), "radius" : 3 * mm, "tangentPropagation" : true, "allowEdgeOverflow" : false});
        }
        {
            var Q0;
            Q0=makeQuery(id+"F3.opExtrude","CAP_FACE",FACE,{"disambiguationData":[OSD([sQuery(id+"F2.wireOp",EDGE,"E0.bottom"),sQuery(id+"F2.wireOp",EDGE,"E0.top"),sQuery(id+"F2.wireOp",EDGE,"E0.left"),sQuery(id+"F2.wireOp",EDGE,"E0.right"),sQuery(id+"F2.wireOp",EDGE,"E1.top"),sQuery(id+"F2.wireOp",EDGE,"E1.left"),sQuery(id+"F2.wireOp",EDGE,"E1.right"),sQuery(id+"F2.wireOp",EDGE,"E2"),sQuery(id+"F2.wireOp",EDGE,"E3"),sQuery(id+"F2.wireOp",EDGE,"E4")])],"isStart":true});
            var sketch = newSketch(context, id + "F54", { "sketchPlane" : qUnion([Q0])});
            skLineSegment(sketch, "E115.bottom", {"start": v(26.97, 2.55) * mm, "end": v(27.97, 2.55) * mm});
            skLineSegment(sketch, "E115.top", {"start": v(26.97, -6.77) * mm, "end": v(27.97, -6.77) * mm});
            skLineSegment(sketch, "E115.left", {"start": v(26.97, 2.55) * mm, "end": v(26.97, -6.77) * mm});
            skLineSegment(sketch, "E115.right", {"start": v(27.97, 2.55) * mm, "end": v(27.97, -6.77) * mm});
            skLineSegment(sketch, "E116.bottom", {"start": v(53.47, -11.77) * mm, "end": v(62.22, -11.77) * mm});
            skLineSegment(sketch, "E116.top", {"start": v(53.47, -12.77) * mm, "end": v(62.22, -12.77) * mm});
            skLineSegment(sketch, "E116.left", {"start": v(53.47, -11.77) * mm, "end": v(53.47, -12.77) * mm});
            skLineSegment(sketch, "E116.right", {"start": v(62.22, -11.77) * mm, "end": v(62.22, -12.77) * mm});
            skLineSegment(sketch, "E117.bottom", {"start": v(54.34, -27.76) * mm, "end": v(62.82, -27.76) * mm});
            skLineSegment(sketch, "E117.top", {"start": v(54.34, -28.76) * mm, "end": v(62.82, -28.76) * mm});
            skLineSegment(sketch, "E117.left", {"start": v(54.34, -27.76) * mm, "end": v(54.34, -28.76) * mm});
            skLineSegment(sketch, "E117.right", {"start": v(62.82, -27.76) * mm, "end": v(62.82, -28.76) * mm});
            skSolve(sketch);
        }
        {
            var Q0;
            Q0=makeQuery(id+"F5.opExtrude","SWEPT_FACE",FACE,{"disambiguationData":[OSD([sQuery(id+"F4.wireOp",EDGE,"E11")])]});
            var sketch = newSketch(context, id + "F55", { "sketchPlane" : qUnion([Q0])});
            skLineSegment(sketch, "E118", {"start": v(6, 5) * mm, "end": v(12, -1) * mm});
            skLineSegment(sketch, "E119", {"start": v(12, -1) * mm, "end": v(28, -1) * mm});
            skLineSegment(sketch, "E120", {"start": v(28, -1) * mm, "end": v(34, 5) * mm});
            skLineSegment(sketch, "E121", {"start": v(34, 5) * mm, "end": v(6, 5) * mm});
            skSolve(sketch);
        }
        {
            var Q0;
            Q0 = qSketchRegion(id + "F55", true);
            extrude(context, id + "F56", {"entities" : qUnion([Q0]), "operationType" : NewBodyOperationType.REMOVE, "depth" : 35 * mm, "offsetDistance" : 25 * mm});
        }
    });
